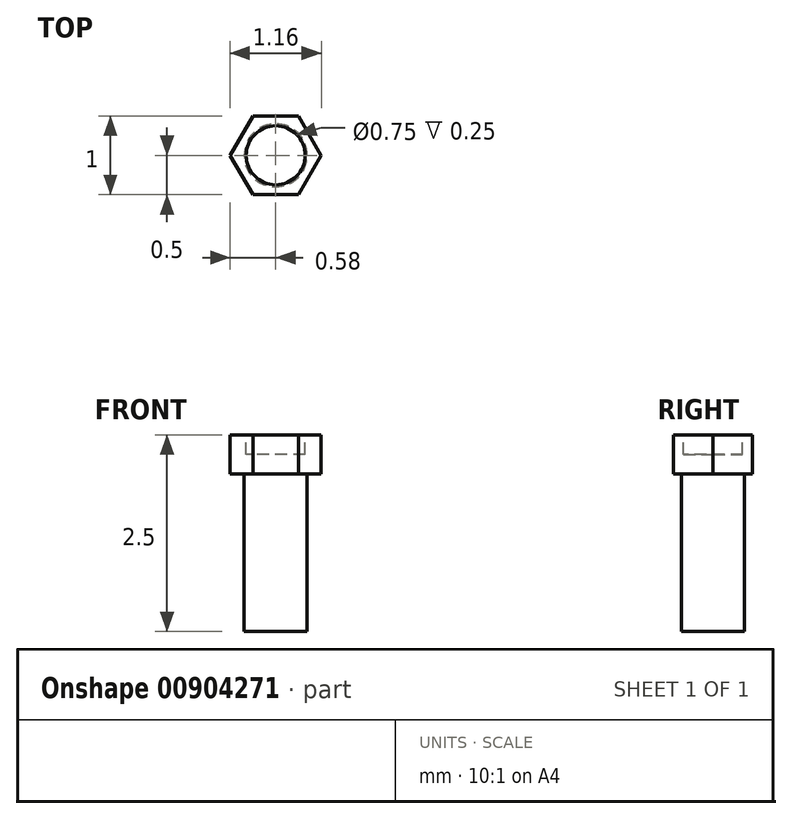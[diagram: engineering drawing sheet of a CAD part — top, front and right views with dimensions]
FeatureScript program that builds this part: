
annotation { "Feature Type Name" : "Feature", "Feature Type Description" : "" }
export const myFeature = defineFeature(function(context is Context, id is Id, definition is map)
    precondition{}
    {
        {
            var Q0;
            Q0=qCreatedBy(makeId("Front.planeOp"),FACE);
            var sketch = newSketch(context, id + "F0", { "sketchPlane" : qUnion([Q0])});
            skLineSegment(sketch, "E0.bottom", {"start": v(0, 0) * mm, "end": v(-0.4, 0) * mm});
            skLineSegment(sketch, "E0.top", {"start": v(0, 2) * mm, "end": v(-0.4, 2) * mm});
            skLineSegment(sketch, "E0.left", {"start": v(0, 0) * mm, "end": v(0, 2) * mm});
            skLineSegment(sketch, "E0.right", {"start": v(-0.4, 0) * mm, "end": v(-0.4, 2) * mm});
            skSolve(sketch);
        }
        {
            var Q0;
            Q0=makeQuery(id+"F0.imprint","IMPRINT",FACE,{"disambiguationData":[TD([[makeQuery(id+"F0.imprint","IMPRINT",EDGE,{"derivedFrom":sQuery(id+"F0.wireOp",EDGE,"E0.bottom")}),-1.0]])]});
            var Q1;
            Q1=sQuery(id+"F0.wireOp",EDGE,"E0.left");
            revolve(context, id + "F1", {"surfaceOperationType" : NewSurfaceOperationType.NEW, "entities" : qUnion([Q0]), "axis" : qUnion([Q1]), "revolveType" : RevolveType.FULL});
        }
        {
            var Q0;
            Q0=makeQuery(id+"F1.opRevolve","SWEPT_FACE",FACE,{"disambiguationData":[OSD([sQuery(id+"F0.wireOp",EDGE,"E0.top")])]});
            var sketch = newSketch(context, id + "F2", { "sketchPlane" : qUnion([Q0])});
            skCircle(sketch, "E1.cCircle", {"center": v(0, 0) * mm, "radius": 0.5 * mm, "construction": true});
            skLineSegment(sketch, "E1.0", {"start": v(-0.29, 0.5) * mm, "end": v(0.29, 0.5) * mm});
            skLineSegment(sketch, "E1.1", {"start": v(0.29, 0.5) * mm, "end": v(0.58, 0) * mm});
            skLineSegment(sketch, "E1.2", {"start": v(0.58, 0) * mm, "end": v(0.29, -0.5) * mm});
            skLineSegment(sketch, "E1.3", {"start": v(0.29, -0.5) * mm, "end": v(-0.29, -0.5) * mm});
            skLineSegment(sketch, "E1.4", {"start": v(-0.29, -0.5) * mm, "end": v(-0.58, 0) * mm});
            skLineSegment(sketch, "E1.5", {"start": v(-0.58, 0) * mm, "end": v(-0.29, 0.5) * mm});
            skPoint(sketch, "E1.0.midPoint", {"position": v(0, 0.5) * mm});
            skSolve(sketch);
        }
        {
            var Q0;
            Q0=makeQuery(id+"F2.imprint","IMPRINT",FACE,{"disambiguationData":[TD([[makeQuery(id+"F2.imprint","IMPRINT",EDGE,{"derivedFrom":sQuery(id+"F2.wireOp",EDGE,"E1.0")}),-1.0]])]});
            var Q1;
            Q1=makeQuery(id+"F2.imprint","IMPRINT",FACE,{"disambiguationData":[TD([[makeQuery(id+"F2.imprint","IMPRINT",EDGE,{"derivedFrom":makeQuery(id+"F1.opRevolve","SWEPT_EDGE",EDGE,{"disambiguationData":[OSD([sQuery(id+"F0.wireOp",EDGE,"E0.top"),sQuery(id+"F0.wireOp",EDGE,"E0.right")])]})}),-1.0]])]});
            extrude(context, id + "F3", {"entities" : qUnion([Q0, Q1]), "operationType" : NewBodyOperationType.ADD, "depth" : 0.5 * mm, "offsetDistance" : 25 * mm});
        }
        {
            var Q0;
            Q0=makeQuery(id+"F3.opExtrude","CAP_FACE",FACE,{"disambiguationData":[OSD([sQuery(id+"F2.wireOp",EDGE,"E1.0"),sQuery(id+"F2.wireOp",EDGE,"E1.1"),sQuery(id+"F2.wireOp",EDGE,"E1.2"),sQuery(id+"F2.wireOp",EDGE,"E1.3"),sQuery(id+"F2.wireOp",EDGE,"E1.4"),sQuery(id+"F2.wireOp",EDGE,"E1.5")])],"isStart":false});
            var sketch = newSketch(context, id + "F4", { "sketchPlane" : qUnion([Q0])});
            skCircle(sketch, "E2", {"center": v(0, 0) * mm, "radius": 0.38 * mm});
            skSolve(sketch);
        }
        {
            var Q0;
            Q0=makeQuery(id+"F4.imprint","IMPRINT",FACE,{"disambiguationData":[TD([[makeQuery(id+"F4.imprint","IMPRINT",EDGE,{"derivedFrom":sQuery(id+"F4.wireOp",EDGE,"E2")}),1.0]])]});
            extrude(context, id + "F5", {"entities" : qUnion([Q0]), "operationType" : NewBodyOperationType.REMOVE, "oppositeDirection" : true, "depth" : 0.25 * mm, "offsetDistance" : 25 * mm});
        }
    });
